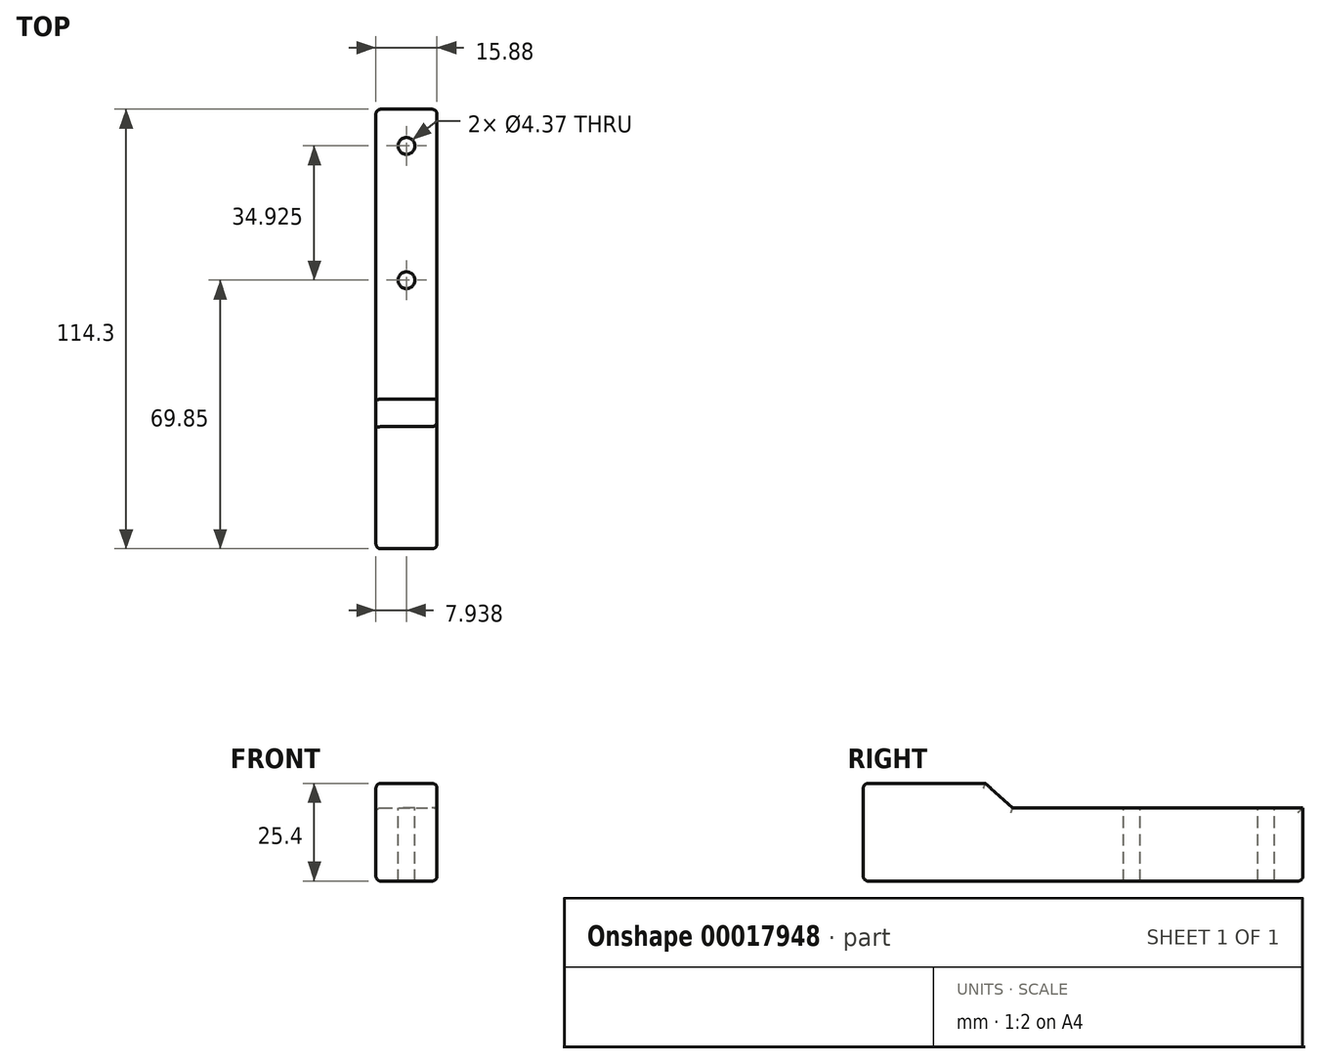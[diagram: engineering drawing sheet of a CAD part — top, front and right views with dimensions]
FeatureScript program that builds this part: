
annotation { "Feature Type Name" : "Feature", "Feature Type Description" : "" }
export const myFeature = defineFeature(function(context is Context, id is Id, definition is map)
    precondition{}
    {
        {
            var Q0;
            Q0=qCreatedBy(makeId("Top.planeOp"),FACE);
            var sketch = newSketch(context, id + "F0", { "sketchPlane" : qUnion([Q0])});
            skLineSegment(sketch, "E0.bottom", {"start": v(0, 0) * mm, "end": v(15.88, 0) * mm});
            skLineSegment(sketch, "E0.top", {"start": v(0, -114.3) * mm, "end": v(15.88, -114.3) * mm});
            skLineSegment(sketch, "E0.left", {"start": v(0, 0) * mm, "end": v(0, -114.3) * mm});
            skLineSegment(sketch, "E0.right", {"start": v(15.88, 0) * mm, "end": v(15.88, -114.3) * mm});
            skSolve(sketch);
        }
        {
            var Q0;
            Q0=makeQuery(id+"F0.imprint","IMPRINT",FACE,{"disambiguationData":[TD([[makeQuery(id+"F0.imprint","IMPRINT",EDGE,{"derivedFrom":sQuery(id+"F0.wireOp",EDGE,"E0.bottom")}),-1.0]])]});
            extrude(context, id + "F1", {"entities" : qUnion([Q0]), "depth" : 25.4 * mm});
        }
        {
            var Q0;
            Q0=makeQuery(id+"F1.opExtrude","SWEPT_FACE",FACE,{"disambiguationData":[OSD([sQuery(id+"F0.wireOp",EDGE,"E0.right")])]});
            var sketch = newSketch(context, id + "F2", { "sketchPlane" : qUnion([Q0])});
            skLineSegment(sketch, "E1", {"start": v(0, 19.05) * mm, "end": v(-75.4, 19.05) * mm});
            skLineSegment(sketch, "E2", {"start": v(-75.4, 19.05) * mm, "end": v(-82.55, 25.4) * mm});
            skSolve(sketch);
        }
        {
            var Q0;
            {var subQ0=sQuery(id+"F2.wireOp",EDGE,"E1");Q0=makeQuery(id+"F2.imprint","IMPRINT",FACE,{"disambiguationData":[TD([[makeQuery(id+"F2.imprint","IMPRINT",EDGE,{"derivedFrom":subQ0}),-1.0]])]});}
            extrude(context, id + "F3", {"entities" : qUnion([Q0]), "operationType" : NewBodyOperationType.REMOVE, "oppositeDirection" : true, "depth" : 25.4 * mm});
        }
        {
            var Q0;
            Q0=makeQuery(id+"F3.boolean.opBoolean","COPY",FACE,{"derivedFrom":makeQuery(id+"F3.opExtrude","SWEPT_FACE",FACE,{"disambiguationData":[OSD([sQuery(id+"F2.wireOp",EDGE,"E1")])]})});
            var sketch = newSketch(context, id + "F4", { "sketchPlane" : qUnion([Q0])});
            skCircle(sketch, "E3", {"center": v(7.94, -9.53) * mm, "radius": 2.18 * mm});
            skPoint(sketch, "E3.centerSnap0", {"position": v(7.94, 0) * mm});
            skCircle(sketch, "E4", {"center": v(7.94, -44.45) * mm, "radius": 2.18 * mm});
            skSolve(sketch);
        }
        {
            var Q0;
            Q0=makeQuery(id+"F4.imprint","IMPRINT",FACE,{"disambiguationData":[TD([[makeQuery(id+"F4.imprint","IMPRINT",EDGE,{"derivedFrom":sQuery(id+"F4.wireOp",EDGE,"E3")}),1.0]])]});
            var Q1;
            Q1=makeQuery(id+"F4.imprint","IMPRINT",FACE,{"disambiguationData":[TD([[makeQuery(id+"F4.imprint","IMPRINT",EDGE,{"derivedFrom":sQuery(id+"F4.wireOp",EDGE,"E4")}),1.0]])]});
            extrude(context, id + "F5", {"entities" : qUnion([Q0, Q1]), "operationType" : NewBodyOperationType.REMOVE, "oppositeDirection" : true, "depth" : 25.4 * mm});
        }
        {
            var Q0;
            Q0=makeQuery(id+"F1.opExtrude","CAP_EDGE",EDGE,{"disambiguationData":[OSD([sQuery(id+"F0.wireOp",EDGE,"E0.top")])],"isStart":true});
            var Q1;
            Q1=makeQuery(id+"F1.opExtrude","SWEPT_EDGE",EDGE,{"disambiguationData":[OSD([sQuery(id+"F0.wireOp",EDGE,"E0.top"),sQuery(id+"F0.wireOp",EDGE,"E0.left")])]});
            var Q2;
            Q2=makeQuery(id+"F1.opExtrude","SWEPT_EDGE",EDGE,{"disambiguationData":[OSD([sQuery(id+"F0.wireOp",EDGE,"E0.top"),sQuery(id+"F0.wireOp",EDGE,"E0.right")])]});
            var Q3;
            Q3=makeQuery(id+"F1.opExtrude","CAP_EDGE",EDGE,{"disambiguationData":[OSD([sQuery(id+"F0.wireOp",EDGE,"E0.top")])],"isStart":false});
            var Q4;
            Q4=makeQuery(id+"F1.opExtrude","CAP_EDGE",EDGE,{"disambiguationData":[OSD([sQuery(id+"F0.wireOp",EDGE,"E0.left")])],"isStart":true});
            var Q5;
            Q5=makeQuery(id+"F1.opExtrude","CAP_EDGE",EDGE,{"disambiguationData":[OSD([sQuery(id+"F0.wireOp",EDGE,"E0.right")])],"isStart":true});
            var Q6;
            Q6=makeQuery(id+"F1.opExtrude","CAP_EDGE",EDGE,{"disambiguationData":[OSD([sQuery(id+"F0.wireOp",EDGE,"E0.bottom")])],"isStart":true});
            var Q7;
            Q7=makeQuery(id+"F3.boolean.opBoolean","INTERSECT",EDGE,{"derivedFrom":[makeQuery(id+"F1.opExtrude","SWEPT_FACE",FACE,{"disambiguationData":[OSD([sQuery(id+"F0.wireOp",EDGE,"E0.left")])]}),makeQuery(id+"F3.opExtrude","SWEPT_FACE",FACE,{"disambiguationData":[OSD([sQuery(id+"F2.wireOp",EDGE,"E1")])]})]});
            var Q8;
            Q8=makeQuery(id+"F3.boolean.opBoolean","COPY",EDGE,{"derivedFrom":makeQuery(id+"F3.opExtrude","CAP_EDGE",EDGE,{"disambiguationData":[OSD([sQuery(id+"F2.wireOp",EDGE,"E1")])],"isStart":true})});
            var Q9;
            Q9=makeQuery(id+"F3.boolean.opBoolean","COPY",EDGE,{"derivedFrom":makeQuery(id+"F3.opExtrude","SWEPT_EDGE",EDGE,{"disambiguationData":[OSD([sQuery(id+"F0.wireOp",EDGE,"E0.bottom"),sQuery(id+"F0.wireOp",EDGE,"E0.right"),sQuery(id+"F2.wireOp",EDGE,"E1")])]})});
            var Q10;
            Q10=makeQuery(id+"F1.opExtrude","SWEPT_EDGE",EDGE,{"disambiguationData":[OSD([sQuery(id+"F0.wireOp",EDGE,"E0.bottom"),sQuery(id+"F0.wireOp",EDGE,"E0.right")])]});
            var Q11;
            Q11=makeQuery(id+"F1.opExtrude","SWEPT_EDGE",EDGE,{"disambiguationData":[OSD([sQuery(id+"F0.wireOp",EDGE,"E0.bottom"),sQuery(id+"F0.wireOp",EDGE,"E0.left")])]});
            var Q12;
            Q12=makeQuery(id+"F3.boolean.opBoolean","INTERSECT",EDGE,{"derivedFrom":[makeQuery(id+"F1.opExtrude","SWEPT_FACE",FACE,{"disambiguationData":[OSD([sQuery(id+"F0.wireOp",EDGE,"E0.left")])]}),makeQuery(id+"F3.opExtrude","SWEPT_FACE",FACE,{"disambiguationData":[OSD([sQuery(id+"F2.wireOp",EDGE,"E2")])]})]});
            var Q13;
            Q13=makeQuery(id+"F3.boolean.opBoolean","COPY",EDGE,{"derivedFrom":makeQuery(id+"F3.opExtrude","SWEPT_EDGE",EDGE,{"disambiguationData":[OSD([sQuery(id+"F0.wireOp",EDGE,"E0.right"),sQuery(id+"F2.wireOp",EDGE,"E2")])]})});
            var Q14;
            Q14=makeQuery(id+"F3.boolean.opBoolean","COPY",EDGE,{"derivedFrom":makeQuery(id+"F3.opExtrude","CAP_EDGE",EDGE,{"disambiguationData":[OSD([sQuery(id+"F2.wireOp",EDGE,"E2")])],"isStart":true})});
            var Q15;
            Q15=makeQuery(id+"F1.opExtrude","CAP_EDGE",EDGE,{"disambiguationData":[OSD([sQuery(id+"F0.wireOp",EDGE,"E0.right")])],"isStart":false});
            var Q16;
            Q16=makeQuery(id+"F1.opExtrude","CAP_EDGE",EDGE,{"disambiguationData":[OSD([sQuery(id+"F0.wireOp",EDGE,"E0.left")])],"isStart":false});
            fillet(context, id + "F6", {"entities" : qUnion([Q0, Q1, Q2, Q3, Q4, Q5, Q6, Q7, Q8, Q9, Q10, Q11, Q12, Q13, Q14, Q15, Q16]), "radius" : 1.27 * mm, "tangentPropagation" : true, "allowEdgeOverflow" : false});
        }
    });
